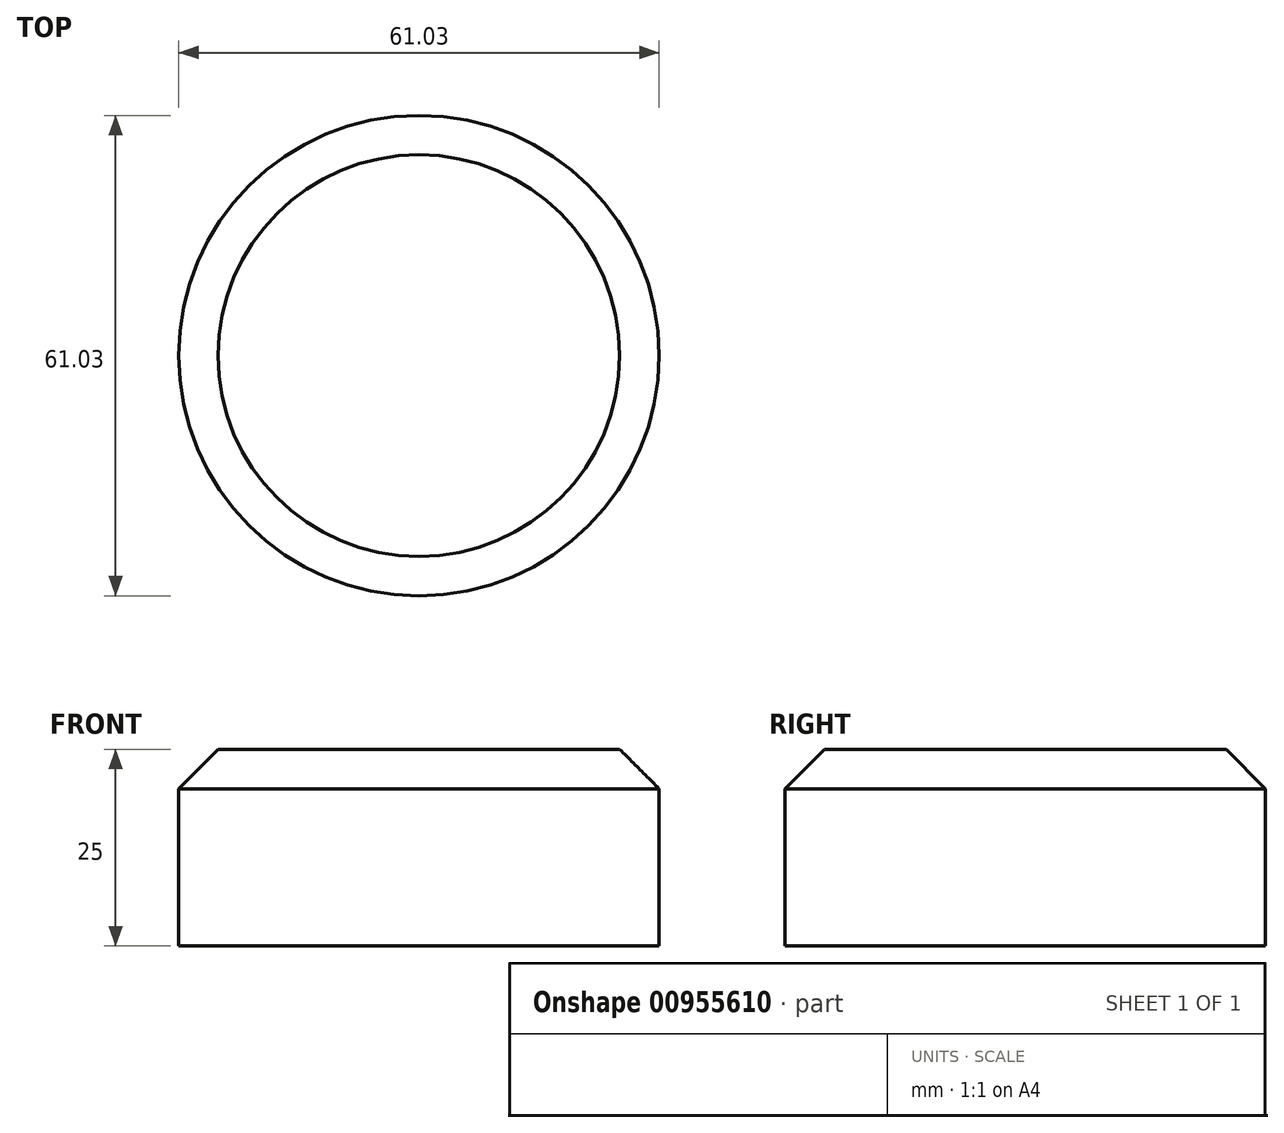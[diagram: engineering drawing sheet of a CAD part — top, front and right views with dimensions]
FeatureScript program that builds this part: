
annotation { "Feature Type Name" : "Feature", "Feature Type Description" : "" }
export const myFeature = defineFeature(function(context is Context, id is Id, definition is map)
    precondition{}
    {
        {
            var Q0;
            Q0=qCreatedBy(makeId("Top.planeOp"),FACE);
            var sketch = newSketch(context, id + "F0", { "sketchPlane" : qUnion([Q0])});
            skCircle(sketch, "E0", {"center": v(-38.99, 42.7) * mm, "radius": 30.51 * mm});
            skSolve(sketch);
        }
        {
            var Q0;
            Q0=makeQuery(id+"F0.imprint","IMPRINT",FACE,{"disambiguationData":[TD([[makeQuery(id+"F0.imprint","IMPRINT",EDGE,{"derivedFrom":sQuery(id+"F0.wireOp",EDGE,"E0")}),1.0]])]});
            extrude(context, id + "F1", {"entities" : qUnion([Q0]), "depth" : 25 * mm, "offsetDistance" : 25 * mm});
        }
        {
            var Q0;
            Q0=makeQuery(id+"F1.opExtrude","CAP_FACE",FACE,{"disambiguationData":[OSD([sQuery(id+"F0.wireOp",EDGE,"E0")])],"isStart":false});
            var sketch = newSketch(context, id + "F2", { "sketchPlane" : qUnion([Q0])});
            skLineSegment(sketch, "E1.bottom", {"start": v(-56.28, 58.15) * mm, "end": v(-21.23, 58.15) * mm});
            skLineSegment(sketch, "E1.top", {"start": v(-56.28, 36.24) * mm, "end": v(-21.23, 36.24) * mm});
            skLineSegment(sketch, "E1.left", {"start": v(-56.28, 58.15) * mm, "end": v(-56.28, 36.24) * mm});
            skLineSegment(sketch, "E1.right", {"start": v(-21.23, 58.15) * mm, "end": v(-21.23, 36.24) * mm});
            skSolve(sketch);
        }
        {
            var Q0;
            Q0=sQuery(id+"F2.wireOp",EDGE,"E1.top");
            var Q1;
            Q1=sQuery(id+"F2.wireOp",EDGE,"E1.bottom");
            extrude(context, id + "F3", {"bodyType" : ToolBodyType.SURFACE, "surfaceEntities" : qUnion([Q0, Q1]), "depth" : 25 * mm, "offsetDistance" : 25 * mm});
        }
        {
            var Q0;
            Q0=makeQuery(id+"F1.opExtrude","CAP_EDGE",EDGE,{"disambiguationData":[OSD([sQuery(id+"F0.wireOp",EDGE,"E0")])],"isStart":false});
            chamfer(context, id + "F4", {"entities" : qUnion([Q0]), "width" : 5 * mm, "tangentPropagation" : true});
        }
    });
